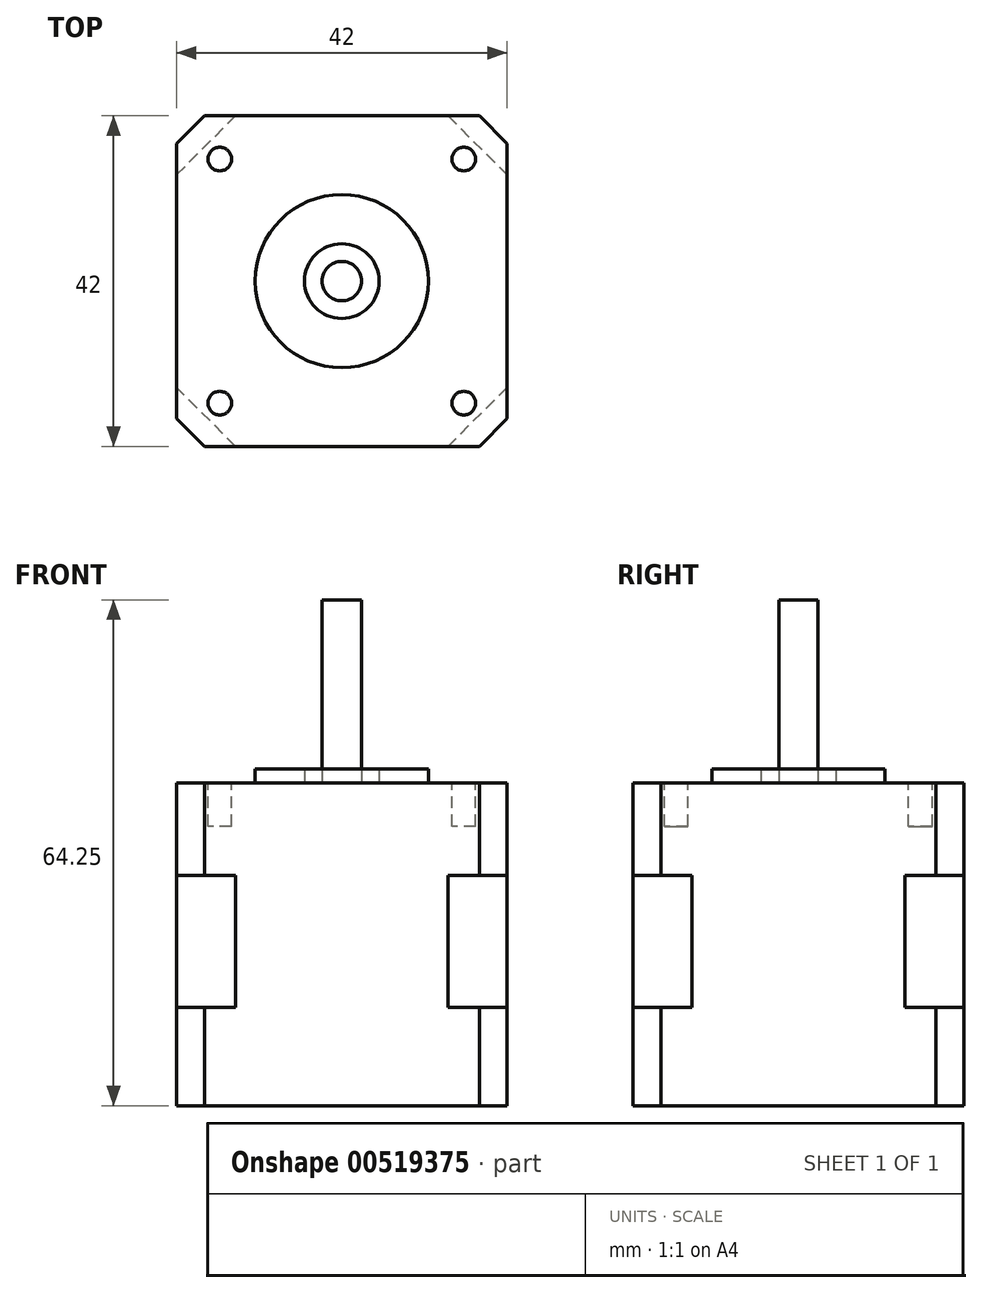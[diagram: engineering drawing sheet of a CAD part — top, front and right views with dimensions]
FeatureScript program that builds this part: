
annotation { "Feature Type Name" : "Feature", "Feature Type Description" : "" }
export const myFeature = defineFeature(function(context is Context, id is Id, definition is map)
    precondition{}
    {
        {
            var Q0;
            Q0=qCreatedBy(makeId("Top.planeOp"),FACE);
            var sketch = newSketch(context, id + "F0", { "sketchPlane" : qUnion([Q0])});
            skLineSegment(sketch, "E0.bottom", {"start": v(-17.46, 21) * mm, "end": v(17.46, 21) * mm});
            skLineSegment(sketch, "E0.top", {"start": v(-17.46, -21) * mm, "end": v(17.46, -21) * mm});
            skLineSegment(sketch, "E0.left", {"start": v(-21, 17.46) * mm, "end": v(-21, -17.46) * mm});
            skLineSegment(sketch, "E0.right", {"start": v(21, 17.46) * mm, "end": v(21, -17.46) * mm});
            skLineSegment(sketch, "E1", {"start": v(-21, -17.46) * mm, "end": v(-17.46, -21) * mm});
            skLineSegment(sketch, "E2", {"start": v(21, -17.46) * mm, "end": v(17.46, -21) * mm});
            skLineSegment(sketch, "E3", {"start": v(-17.46, 21) * mm, "end": v(-21, 17.46) * mm});
            skLineSegment(sketch, "E4", {"start": v(17.46, 21) * mm, "end": v(21, 17.46) * mm});
            skSolve(sketch);
        }
        {
            var Q0;
            Q0=makeQuery(id+"F0.imprint","IMPRINT",FACE,{"disambiguationData":[TD([[makeQuery(id+"F0.imprint","IMPRINT",EDGE,{"derivedFrom":sQuery(id+"F0.wireOp",EDGE,"E0.bottom")}),-1.0]])]});
            extrude(context, id + "F1", {"entities" : qUnion([Q0]), "depth" : 12.5 * mm, "offsetDistance" : 25 * mm});
        }
        {
            var Q0;
            Q0=makeQuery(id+"F1.opExtrude","CAP_FACE",FACE,{"disambiguationData":[OSD([sQuery(id+"F0.wireOp",EDGE,"E0.bottom"),sQuery(id+"F0.wireOp",EDGE,"E0.top"),sQuery(id+"F0.wireOp",EDGE,"E0.left"),sQuery(id+"F0.wireOp",EDGE,"E0.right"),sQuery(id+"F0.wireOp",EDGE,"E1"),sQuery(id+"F0.wireOp",EDGE,"E2"),sQuery(id+"F0.wireOp",EDGE,"E3"),sQuery(id+"F0.wireOp",EDGE,"E4")])],"isStart":false});
            var sketch = newSketch(context, id + "F2", { "sketchPlane" : qUnion([Q0])});
            skLineSegment(sketch, "E5", {"start": v(-13.5, 21) * mm, "end": v(13.5, 21) * mm});
            skLineSegment(sketch, "E6", {"start": v(13.5, 21) * mm, "end": v(21, 13.5) * mm});
            skLineSegment(sketch, "E7", {"start": v(21, 13.5) * mm, "end": v(21, -13.5) * mm});
            skLineSegment(sketch, "E8", {"start": v(21, -13.5) * mm, "end": v(13.5, -21) * mm});
            skLineSegment(sketch, "E9", {"start": v(13.5, -21) * mm, "end": v(-13.5, -21) * mm});
            skLineSegment(sketch, "E10", {"start": v(-13.5, -21) * mm, "end": v(-21, -13.5) * mm});
            skLineSegment(sketch, "E11", {"start": v(-21, -13.5) * mm, "end": v(-21, 13.5) * mm});
            skLineSegment(sketch, "E12", {"start": v(-21, 13.5) * mm, "end": v(-13.5, 21) * mm});
            skSolve(sketch);
        }
        {
            var Q0;
            Q0 = qSketchRegion(id + "F2", true);
            extrude(context, id + "F3", {"entities" : qUnion([Q0]), "operationType" : NewBodyOperationType.ADD, "depth" : 16.75 * mm, "offsetDistance" : 25 * mm});
        }
        {
            var Q0;
            Q0 = qSketchRegion(id + "F0", true);
            extrude(context, id + "F4", {"entities" : qUnion([Q0]), "operationType" : NewBodyOperationType.ADD, "depth" : 41 * mm, "offsetDistance" : 25 * mm, "hasSecondDirection" : true, "secondDirectionOppositeDirection" : false, "secondDirectionDepth" : 29.25 * mm});
        }
        {
            var Q0;
            Q0=makeQuery(id+"F4.opExtrude","CAP_FACE",FACE,{"disambiguationData":[OSD([sQuery(id+"F0.wireOp",EDGE,"E0.bottom"),sQuery(id+"F0.wireOp",EDGE,"E0.top"),sQuery(id+"F0.wireOp",EDGE,"E0.left"),sQuery(id+"F0.wireOp",EDGE,"E0.right"),sQuery(id+"F0.wireOp",EDGE,"E1"),sQuery(id+"F0.wireOp",EDGE,"E2"),sQuery(id+"F0.wireOp",EDGE,"E3"),sQuery(id+"F0.wireOp",EDGE,"E4")])],"isStart":false});
            var sketch = newSketch(context, id + "F5", { "sketchPlane" : qUnion([Q0])});
            skCircle(sketch, "E13", {"center": v(-15.5, 15.5) * mm, "radius": 1.5 * mm});
            skCircle(sketch, "E14", {"center": v(15.5, 15.5) * mm, "radius": 1.5 * mm});
            skCircle(sketch, "E15", {"center": v(15.5, -15.5) * mm, "radius": 1.5 * mm});
            skCircle(sketch, "E16", {"center": v(-15.5, -15.5) * mm, "radius": 1.5 * mm});
            skSolve(sketch);
        }
        {
            var Q0;
            Q0 = qSketchRegion(id + "F5", true);
            extrude(context, id + "F6", {"entities" : qUnion([Q0]), "operationType" : NewBodyOperationType.REMOVE, "oppositeDirection" : true, "depth" : 5.5 * mm, "offsetDistance" : 25 * mm});
        }
        {
            var Q0;
            Q0=makeQuery(id+"F4.opExtrude","CAP_FACE",FACE,{"disambiguationData":[OSD([sQuery(id+"F0.wireOp",EDGE,"E0.bottom"),sQuery(id+"F0.wireOp",EDGE,"E0.top"),sQuery(id+"F0.wireOp",EDGE,"E0.left"),sQuery(id+"F0.wireOp",EDGE,"E0.right"),sQuery(id+"F0.wireOp",EDGE,"E1"),sQuery(id+"F0.wireOp",EDGE,"E2"),sQuery(id+"F0.wireOp",EDGE,"E3"),sQuery(id+"F0.wireOp",EDGE,"E4")])],"isStart":false});
            var sketch = newSketch(context, id + "F7", { "sketchPlane" : qUnion([Q0])});
            skCircle(sketch, "E17", {"center": v(0, 0) * mm, "radius": 11 * mm});
            skCircle(sketch, "E18", {"center": v(0, 0) * mm, "radius": 4.75 * mm});
            skSolve(sketch);
        }
        {
            var Q0;
            Q0 = qSketchRegion(id + "F7", true);
            extrude(context, id + "F8", {"entities" : qUnion([Q0]), "operationType" : NewBodyOperationType.ADD, "depth" : 1.75 * mm, "offsetDistance" : 25 * mm});
        }
        {
            var Q0;
            Q0=makeQuery(id+"F8.boolean.opBoolean","SPLIT",FACE,{"disambiguationData":[TD([makeQuery(id+"F8.opExtrude","SWEPT_FACE",FACE,{"disambiguationData":[OSD([sQuery(id+"F7.wireOp",EDGE,"E18")])]})])],"derivedFrom":makeQuery(id+"F4.opExtrude","CAP_FACE",FACE,{"disambiguationData":[OSD([sQuery(id+"F0.wireOp",EDGE,"E0.bottom"),sQuery(id+"F0.wireOp",EDGE,"E0.top"),sQuery(id+"F0.wireOp",EDGE,"E0.left"),sQuery(id+"F0.wireOp",EDGE,"E0.right"),sQuery(id+"F0.wireOp",EDGE,"E1"),sQuery(id+"F0.wireOp",EDGE,"E2"),sQuery(id+"F0.wireOp",EDGE,"E3"),sQuery(id+"F0.wireOp",EDGE,"E4")])],"isStart":false})});
            var sketch = newSketch(context, id + "F9", { "sketchPlane" : qUnion([Q0])});
            skCircle(sketch, "E19", {"center": v(0, 0) * mm, "radius": 2.5 * mm});
            skSolve(sketch);
        }
        {
            var Q0;
            Q0 = qSketchRegion(id + "F9", true);
            extrude(context, id + "F10", {"entities" : qUnion([Q0]), "operationType" : NewBodyOperationType.ADD, "depth" : (21.5 + 1.75) * mm, "offsetDistance" : 25 * mm});
        }
    });
